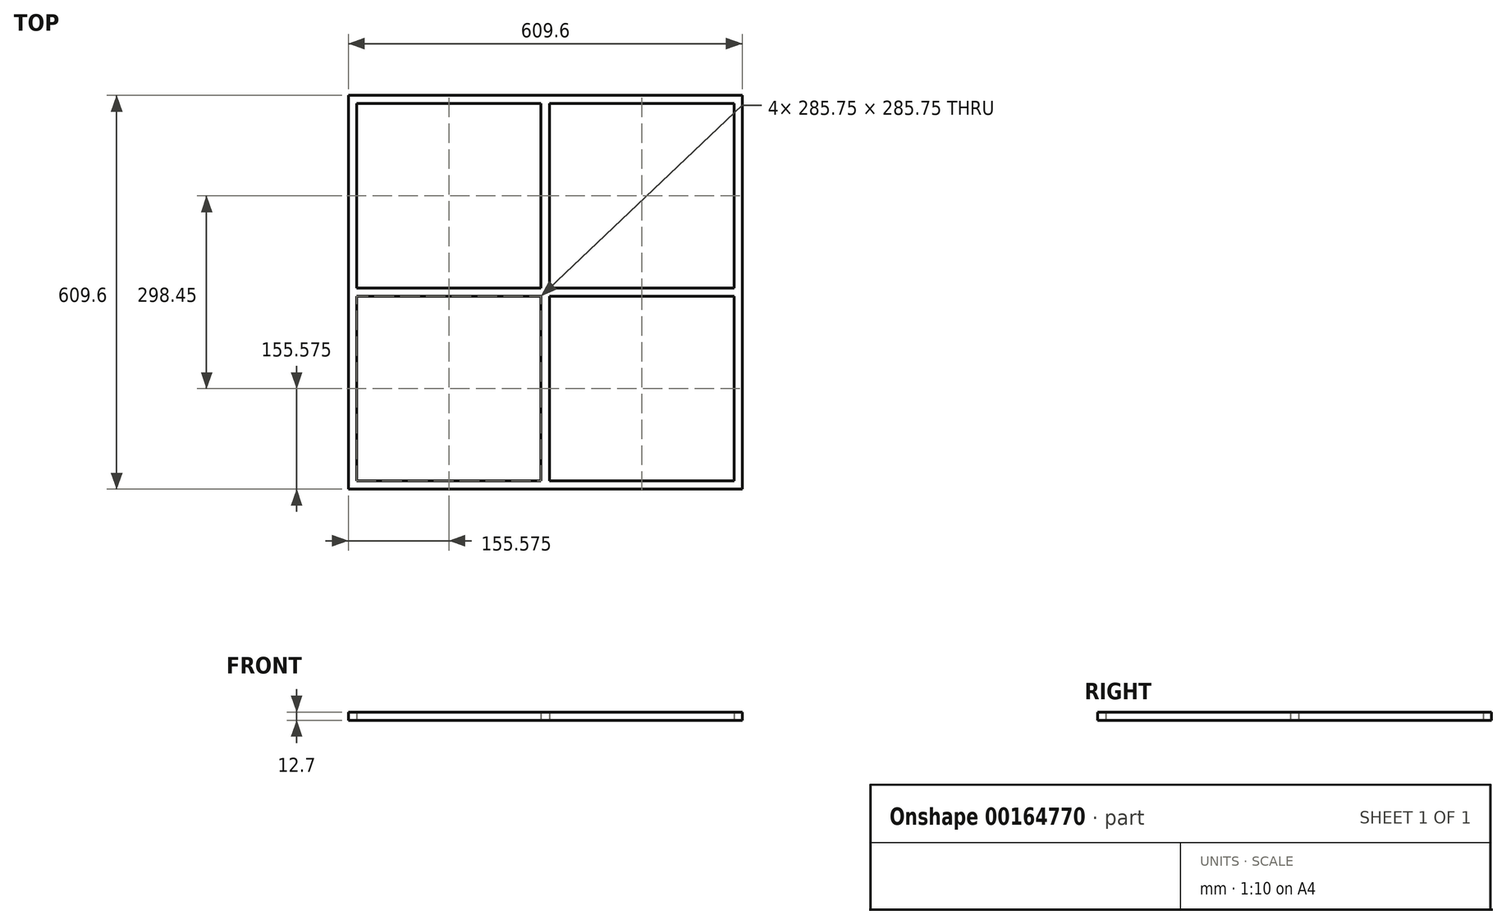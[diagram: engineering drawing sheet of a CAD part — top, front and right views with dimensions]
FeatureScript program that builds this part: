
annotation { "Feature Type Name" : "Feature", "Feature Type Description" : "" }
export const myFeature = defineFeature(function(context is Context, id is Id, definition is map)
    precondition{}
    {
        {
            var Q0;
            Q0=qCreatedBy(makeId("Top.planeOp"),FACE);
            var sketch = newSketch(context, id + "F0", { "sketchPlane" : qUnion([Q0])});
            skLineSegment(sketch, "E0.bottom", {"start": v(304.8, 304.8) * mm, "end": v(-304.8, 304.8) * mm});
            skLineSegment(sketch, "E0.top", {"start": v(304.8, -304.8) * mm, "end": v(-304.8, -304.8) * mm});
            skLineSegment(sketch, "E0.left", {"start": v(304.8, 304.8) * mm, "end": v(304.8, -304.8) * mm});
            skLineSegment(sketch, "E0.right", {"start": v(-304.8, 304.8) * mm, "end": v(-304.8, -304.8) * mm});
            skPoint(sketch, "E0.middle", {"position": v(0, 0) * mm});
            skLineSegment(sketch, "E1.bottom", {"start": v(6.35, 6.35) * mm, "end": v(-6.35, 6.35) * mm, "construction": true});
            skLineSegment(sketch, "E1.top", {"start": v(6.35, -6.35) * mm, "end": v(-6.35, -6.35) * mm, "construction": true});
            skLineSegment(sketch, "E1.left", {"start": v(6.35, 6.35) * mm, "end": v(6.35, -6.35) * mm, "construction": true});
            skLineSegment(sketch, "E1.right", {"start": v(-6.35, 6.35) * mm, "end": v(-6.35, -6.35) * mm, "construction": true});
            skLineSegment(sketch, "E2.bottom", {"start": v(6.35, 6.35) * mm, "end": v(292.1, 6.35) * mm});
            skLineSegment(sketch, "E2.top", {"start": v(6.35, 292.1) * mm, "end": v(292.1, 292.1) * mm});
            skLineSegment(sketch, "E2.left", {"start": v(6.35, 6.35) * mm, "end": v(6.35, 292.1) * mm});
            skLineSegment(sketch, "E2.right", {"start": v(292.1, 6.35) * mm, "end": v(292.1, 292.1) * mm});
            skLineSegment(sketch, "E3.bottom", {"start": v(-6.35, 6.35) * mm, "end": v(-292.1, 6.35) * mm});
            skLineSegment(sketch, "E3.top", {"start": v(-6.35, 292.1) * mm, "end": v(-292.1, 292.1) * mm});
            skLineSegment(sketch, "E3.left", {"start": v(-6.35, 6.35) * mm, "end": v(-6.35, 292.1) * mm});
            skLineSegment(sketch, "E3.right", {"start": v(-292.1, 6.35) * mm, "end": v(-292.1, 292.1) * mm});
            skLineSegment(sketch, "E4.bottom", {"start": v(-6.35, -6.35) * mm, "end": v(-292.1, -6.35) * mm});
            skLineSegment(sketch, "E4.top", {"start": v(-6.35, -292.1) * mm, "end": v(-292.1, -292.1) * mm});
            skLineSegment(sketch, "E4.left", {"start": v(-6.35, -6.35) * mm, "end": v(-6.35, -292.1) * mm});
            skLineSegment(sketch, "E4.right", {"start": v(-292.1, -6.35) * mm, "end": v(-292.1, -292.1) * mm});
            skLineSegment(sketch, "E5.bottom", {"start": v(6.35, -6.35) * mm, "end": v(292.1, -6.35) * mm});
            skLineSegment(sketch, "E5.top", {"start": v(6.35, -292.1) * mm, "end": v(292.1, -292.1) * mm});
            skLineSegment(sketch, "E5.left", {"start": v(6.35, -6.35) * mm, "end": v(6.35, -292.1) * mm});
            skLineSegment(sketch, "E5.right", {"start": v(292.1, -6.35) * mm, "end": v(292.1, -292.1) * mm});
            skLineSegment(sketch, "E6", {"start": v(-292.1, 292.1) * mm, "end": v(-304.8, 292.1) * mm, "construction": true});
            skLineSegment(sketch, "E7", {"start": v(-292.1, 292.1) * mm, "end": v(-292.1, 304.8) * mm, "construction": true});
            skSolve(sketch);
        }
        {
            var Q0;
            Q0 = qSketchRegion(id + "F0", true);
            extrude(context, id + "F1", {"entities" : qUnion([Q0]), "depth" : 12.7 * mm});
        }
    });
